# Revit family: QF_BOURGEAT_Rayonnage_modulaire_étagère_retour_Aluminium
name_source: partatom
category: Equipement spécialisé
revit_build: Autodesk Revit 2015 (Build: 20140606_1530(x64)
units: mm (PartAtom-declared; Revit-internal decimal feet)

## types (1)
- QF_BOURGEAT_Rayonnage_modulaire_étagère_retour_Aluminium
    4 niveaux = Oui
    4 niveaux Plateau 2 = Non
    4 niveaux plateau 3 = Non
    Calagepl2 = 0 mm  [stored 0 ft]
    Calagepl3 = 0 mm  [stored 0 ft]
    CentPl1 = 387 mm
    CentPl2 = 387 mm
    CentPl3 = 387 mm
    Certification = NF hygiene alimentaire
    Clayette = Acier inoxydable
    Element d'angle = Acier inoxydable
    Epaisseur de retour = 415 mm  [stored 1.36155 ft]
    Fabricant = BOURGEAT
    Hauteur hors tout = 1730 mm  [stored 5.67585 ft]
    Jeu = 0 mm  [stored 0 ft]
    LP1 = 1
    LP2 = 0
    LP3 = 0
    Longeron = Acier inoxydable
    Longueur = 1220 mm  [stored 4.00262 ft]
    Longueur Plateau 1 = 758 mm  [stored 2.48688 ft]
    Longueur Plateau 2 = 758 mm  [stored 2.48688 ft]
    Longueur Plateau 3 = 758 mm  [stored 2.48688 ft]
    Longueur entraxe 1 = 773 mm
    Longueur entraxe 2 = 773 mm
    Longueur entraxe 3 = 773 mm
    Longueur hors tout = 1220 mm  [stored 4.00262 ft]
    Longueur longeron 1 = 800 mm  [stored 2.62467 ft]
    Longueur longeron 2 = 800 mm  [stored 2.62467 ft]
    Longueur longeron 3 = 800 mm  [stored 2.62467 ft]
    Longueur retour = 805 mm
    Plateau 2 = Non
    Plateau 3 = Non
    Profondeur = 425 mm  [stored 1.39436 ft]
    Profondeur hors tout = 425 mm  [stored 1.39436 ft]
    Spécification du Fabricant = Etagères de Base
    URL catalogue = http://www.bourgeat.fr

note: [stored X ft] marks values corroborated as IEEE doubles in the binary element streams (Revit-internal decimal feet)
